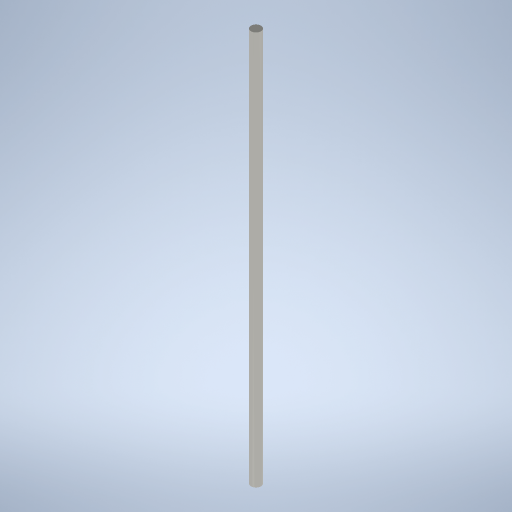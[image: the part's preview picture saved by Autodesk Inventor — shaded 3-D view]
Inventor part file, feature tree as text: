
AUTODESK INVENTOR PART (.ipt)
format: ipt  version: 2024.2 (Build 282272000, 272)  size: 237,056 bytes
history: native  units: mm
features: other x3, extrude x1, sketch x1
ambient origin geometry x8: Origin, YZ Plane, XZ Plane, XY Plane, X Axis, Y Axis, Z Axis, Center Point
bodies: Body1 (feature_tree)
feature tree (5):
  other  "Bryła1"
  extrude  "Wyciągnięcie proste1"  Depth=6.0mm
  sketch  "Szkic1"
  other  "Finish1"
  other  "Finish2"
